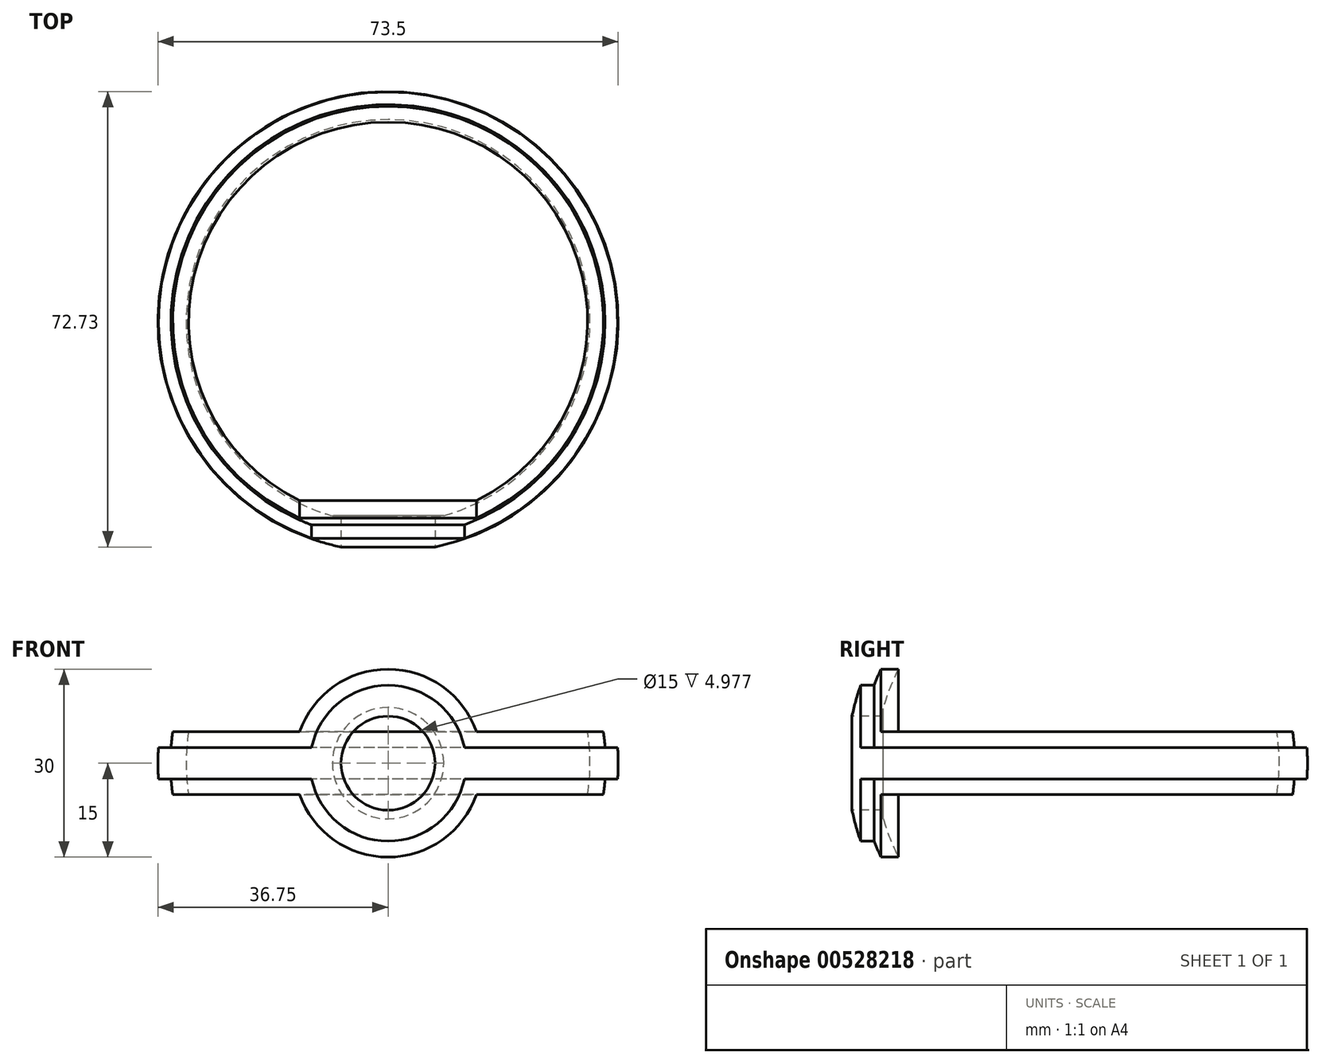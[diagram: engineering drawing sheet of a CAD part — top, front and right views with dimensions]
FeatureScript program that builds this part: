
annotation { "Feature Type Name" : "Feature", "Feature Type Description" : "" }
export const myFeature = defineFeature(function(context is Context, id is Id, definition is map)
    precondition{}
    {
        {
            var Q0;
            Q0=qCreatedBy(makeId("Front.planeOp"),FACE);
            var sketch = newSketch(context, id + "F0", { "sketchPlane" : qUnion([Q0])});
            skArc(sketch, "E0", {"start": v(0, -34.75) * mm, "mid": v(34.75, 0) * mm, "end": v(0, 34.75) * mm});
            skArc(sketch, "E1", {"start": v(0, -32.25) * mm, "mid": v(32.25, 0) * mm, "end": v(0, 32.25) * mm});
            skLineSegment(sketch, "E2", {"start": v(0, -32.25) * mm, "end": v(0, 32.25) * mm, "construction": true});
            skLineSegment(sketch, "E3", {"start": v(0, 34.75) * mm, "end": v(0, 32.25) * mm});
            skLineSegment(sketch, "E4", {"start": v(0, -32.25) * mm, "end": v(0, -34.75) * mm});
            skSolve(sketch);
        }
        {
            var Q0;
            Q0=makeQuery(id+"F0.imprint","IMPRINT",FACE,{"disambiguationData":[TD([[makeQuery(id+"F0.imprint","IMPRINT",EDGE,{"derivedFrom":sQuery(id+"F0.wireOp",EDGE,"E0")}),1.0]])]});
            var Q1;
            Q1=sQuery(id+"F0.wireOp",EDGE,"ArqTZGTh-E7ZS-kiQA-TmLm-oTuQENo7wEDL");
            var Q2;
            Q2=sQuery(id+"F0.wireOp",EDGE,"E0");
            var Q3;
            Q3=sQuery(id+"F0.wireOp",EDGE,"E2");
            revolve(context, id + "F1", {"entities" : qUnion([Q0]), "surfaceEntities" : qUnion([Q1, Q2]), "axis" : qUnion([Q3]), "revolveType" : RevolveType.FULL});
        }
        {
            var Q0;
            Q0=qCreatedBy(makeId("Front.planeOp"),FACE);
            var sketch = newSketch(context, id + "F2", { "sketchPlane" : qUnion([Q0])});
            skLineSegment(sketch, "E5", {"start": v(0, 0) * mm, "end": v(0, 5) * mm, "construction": true});
            skLineSegment(sketch, "E6.bottom", {"start": v(14.14, 5) * mm, "end": v(47.83, 5) * mm});
            skLineSegment(sketch, "E6.top", {"start": v(0, 37.93) * mm, "end": v(47.83, 37.93) * mm});
            skLineSegment(sketch, "E6.left", {"start": v(0, 15) * mm, "end": v(0, 37.93) * mm});
            skLineSegment(sketch, "E6.right", {"start": v(47.83, 5) * mm, "end": v(47.83, 37.93) * mm});
            skArc(sketch, "E7", {"start": v(14.14, 5) * mm, "mid": v(8.66, 12.25) * mm, "end": v(0, 15) * mm});
            skArc(sketch, "E8.MirrorCS", {"start": v(-14.14, 5) * mm, "mid": v(-8.66, 12.25) * mm, "end": v(0, 15) * mm});
            skLineSegment(sketch, "E9.MirrorCS", {"start": v(-14.14, 5) * mm, "end": v(-47.83, 5) * mm});
            skLineSegment(sketch, "E10.MirrorCS", {"start": v(0, 37.93) * mm, "end": v(-47.83, 37.93) * mm});
            skLineSegment(sketch, "E11.MirrorCS", {"start": v(-47.83, 5) * mm, "end": v(-47.83, 37.93) * mm});
            skLineSegment(sketch, "E12", {"start": v(-53.76, 0) * mm, "end": v(58.67, 0) * mm, "construction": true});
            skLineSegment(sketch, "E13.MirrorCS", {"start": v(-47.83, -5) * mm, "end": v(-47.83, -37.93) * mm});
            skLineSegment(sketch, "E14.MirrorCS", {"start": v(-14.14, -5) * mm, "end": v(-47.83, -5) * mm});
            skArc(sketch, "E15.MirrorCS", {"start": v(-14.14, -5) * mm, "mid": v(-8.66, -12.25) * mm, "end": v(0, -15) * mm});
            skArc(sketch, "E16.MirrorCS", {"start": v(14.14, -5) * mm, "mid": v(8.66, -12.25) * mm, "end": v(0, -15) * mm});
            skLineSegment(sketch, "E17.MirrorCS", {"start": v(0, -37.93) * mm, "end": v(-47.83, -37.93) * mm});
            skLineSegment(sketch, "E18.MirrorCS", {"start": v(0, -37.93) * mm, "end": v(47.83, -37.93) * mm});
            skLineSegment(sketch, "E19.MirrorCS", {"start": v(14.14, -5) * mm, "end": v(47.83, -5) * mm});
            skLineSegment(sketch, "E20.MirrorCS", {"start": v(47.83, -5) * mm, "end": v(47.83, -37.93) * mm});
            skSolve(sketch);
        }
        {
            var Q0;
            Q0 = qSketchRegion(id + "F2", true);
            extrude(context, id + "F3", {"entities" : qUnion([Q0]), "operationType" : NewBodyOperationType.REMOVE, "endBound" : BoundingType.THROUGH_ALL, "oppositeDirection" : true, "depth" : 25 * mm, "offsetDistance" : 25 * mm, "hasSecondDirection" : true, "secondDirectionBound" : SecondDirectionBoundingType.THROUGH_ALL, "secondDirectionOppositeDirection" : false, "secondDirectionDepth" : 25 * mm});
        }
        {
            var Q0;
            Q0=qCreatedBy(makeId("Right.planeOp"),FACE);
            var sketch = newSketch(context, id + "F4", { "sketchPlane" : qUnion([Q0])});
            skLineSegment(sketch, "E21.0.1", {"start": v(31.35, 5) * mm, "end": v(28.55, 5) * mm});
            skLineSegment(sketch, "E21.0.2", {"start": v(28.55, 5) * mm, "end": v(28.55, 15) * mm});
            skLineSegment(sketch, "E21.0.3", {"start": v(28.55, 5) * mm, "end": v(31.35, 5) * mm});
            skLineSegment(sketch, "E22.bottom", {"start": v(31.35, 15) * mm, "end": v(38.37, 15) * mm});
            skLineSegment(sketch, "E22.top", {"start": v(31.35, 5) * mm, "end": v(38.37, 5) * mm});
            skLineSegment(sketch, "E22.right", {"start": v(38.37, 15) * mm, "end": v(38.37, 5) * mm});
            skLineSegment(sketch, "E23", {"start": v(31.35, 15) * mm, "end": v(28.55, 15) * mm});
            skLineSegment(sketch, "E24", {"start": v(0, 27.33) * mm, "end": v(0, 0) * mm, "construction": true});
            skLineSegment(sketch, "E25", {"start": v(0, 0) * mm, "end": v(59.24, 0) * mm, "construction": true});
            skLineSegment(sketch, "E26.MirrorCS", {"start": v(31.35, -5) * mm, "end": v(28.55, -5) * mm});
            skLineSegment(sketch, "E27.MirrorCS", {"start": v(31.35, -5) * mm, "end": v(38.37, -5) * mm});
            skLineSegment(sketch, "E28.MirrorCS", {"start": v(28.55, -5) * mm, "end": v(28.55, -15) * mm});
            skLineSegment(sketch, "E29.MirrorCS", {"start": v(28.55, -5) * mm, "end": v(31.35, -5) * mm});
            skLineSegment(sketch, "E30.MirrorCS", {"start": v(31.35, -15) * mm, "end": v(28.55, -15) * mm});
            skLineSegment(sketch, "E31.MirrorCS", {"start": v(31.35, -15) * mm, "end": v(38.37, -15) * mm});
            skLineSegment(sketch, "E32.MirrorCS", {"start": v(38.37, -15) * mm, "end": v(38.37, -5) * mm});
            skSolve(sketch);
        }
        {
            var Q0;
            Q0 = qSketchRegion(id + "F4", true);
            var Q1;
            Q1=sQuery(id+"F4.wireOp",EDGE,"E24");
            revolve(context, id + "F5", {"operationType" : NewBodyOperationType.REMOVE, "entities" : qUnion([Q0]), "axis" : qUnion([Q1]), "revolveType" : RevolveType.TWO_DIRECTIONS, "oppositeDirection" : true, "angle" : 30 * degree, "angleBack" : 330 * degree});
        }
        {
            var Q0;
            Q0=qCreatedBy(makeId("Front.planeOp"),FACE);
            var sketch = newSketch(context, id + "F6", { "sketchPlane" : qUnion([Q0])});
            skLineSegment(sketch, "E33.0", {"start": v(-34.39, 5) * mm, "end": v(34.39, 5) * mm, "construction": true});
            skArc(sketch, "E33.1", {"start": v(0, -34.75) * mm, "mid": v(34.75, 0) * mm, "end": v(0, 34.75) * mm, "construction": true});
            skLineSegment(sketch, "E34", {"start": v(34.75, 0) * mm, "end": v(36.75, 0) * mm});
            skPoint(sketch, "E34.endSnap0", {"position": v(34.75, 0) * mm});
            skLineSegment(sketch, "E35.bottom", {"start": v(36.75, 0) * mm, "end": v(33.58, 0) * mm, "construction": true});
            skLineSegment(sketch, "E35.top", {"start": v(36.75, 2.5) * mm, "end": v(33.58, 2.5) * mm});
            skLineSegment(sketch, "E35.left", {"start": v(36.75, 0) * mm, "end": v(36.75, 2.5) * mm});
            skLineSegment(sketch, "E35.right", {"start": v(33.58, 0) * mm, "end": v(33.58, 2.5) * mm});
            skLineSegment(sketch, "E36.MirrorCS", {"start": v(36.75, 0) * mm, "end": v(36.75, -2.5) * mm});
            skLineSegment(sketch, "E37.MirrorCS", {"start": v(33.58, 0) * mm, "end": v(33.58, -2.5) * mm});
            skLineSegment(sketch, "E38.MirrorCS", {"start": v(36.75, -2.5) * mm, "end": v(33.58, -2.5) * mm});
            skSolve(sketch);
        }
        {
            var Q0;
            Q0=qCreatedBy(makeId("Front.planeOp"),FACE);
            cPlane(context, id + "F7", {"entities" : qUnion([Q0]), "cplaneType" : CPlaneType.OFFSET, "offset" : 31 * mm, "width" : 150 * mm, "height" : 150 * mm});
        }
        {
            var Q0;
            Q0 = qSketchRegion(id + "F6", true);
            var Q1;
            Q1=sQuery(id+"F0.wireOp",EDGE,"E2");
            revolve(context, id + "F8", {"operationType" : NewBodyOperationType.ADD, "entities" : qUnion([Q0]), "axis" : qUnion([Q1]), "revolveType" : RevolveType.FULL});
        }
        {
            var Q0;
            Q0=qCreatedBy(id+"F7.planeOp",FACE);
            var sketch = newSketch(context, id + "F9", { "sketchPlane" : qUnion([Q0])});
            skCircle(sketch, "E39", {"center": v(0, 0) * mm, "radius": 12.45 * mm});
            skSolve(sketch);
        }
        {
            var Q0;
            Q0 = qSketchRegion(id + "F9", true);
            extrude(context, id + "F10", {"entities" : qUnion([Q0]), "operationType" : NewBodyOperationType.ADD, "depth" : 8 * mm, "offsetDistance" : 25 * mm});
        }
        {
            var Q0;
            Q0=qCreatedBy(makeId("Right.planeOp"),FACE);
            var sketch = newSketch(context, id + "F11", { "sketchPlane" : qUnion([Q0])});
            skArc(sketch, "E40", {"start": v(0, 36.75) * mm, "mid": v(-36.75, 0) * mm, "end": v(0, -36.75) * mm});
            skArc(sketch, "E41", {"start": v(0, 45.7) * mm, "mid": v(-45.7, 0) * mm, "end": v(0, -45.7) * mm});
            skLineSegment(sketch, "E42", {"start": v(0, 36.75) * mm, "end": v(0, 45.7) * mm});
            skLineSegment(sketch, "E43", {"start": v(0, -36.75) * mm, "end": v(0, -45.7) * mm});
            skSolve(sketch);
        }
        {
            var Q0;
            Q0 = qSketchRegion(id + "F11", true);
            var Q1;
            Q1=sQuery(id+"F0.wireOp",EDGE,"E2");
            revolve(context, id + "F12", {"operationType" : NewBodyOperationType.REMOVE, "entities" : qUnion([Q0]), "axis" : qUnion([Q1]), "revolveType" : RevolveType.FULL, "oppositeDirection" : true});
        }
        {
            var Q0;
            Q0=qCreatedBy(id+"F7.planeOp",FACE);
            var sketch = newSketch(context, id + "F13", { "sketchPlane" : qUnion([Q0])});
            skCircle(sketch, "E44", {"center": v(0, 0) * mm, "radius": 7.5 * mm});
            skSolve(sketch);
        }
        {
            var Q0;
            Q0 = qSketchRegion(id + "F13", true);
            extrude(context, id + "F14", {"entities" : qUnion([Q0]), "operationType" : NewBodyOperationType.REMOVE, "oppositeDirection" : true, "depth" : 10 * mm, "offsetDistance" : 25 * mm, "hasSecondDirection" : true, "secondDirectionOppositeDirection" : false, "secondDirectionDepth" : 10 * mm});
        }
    });
